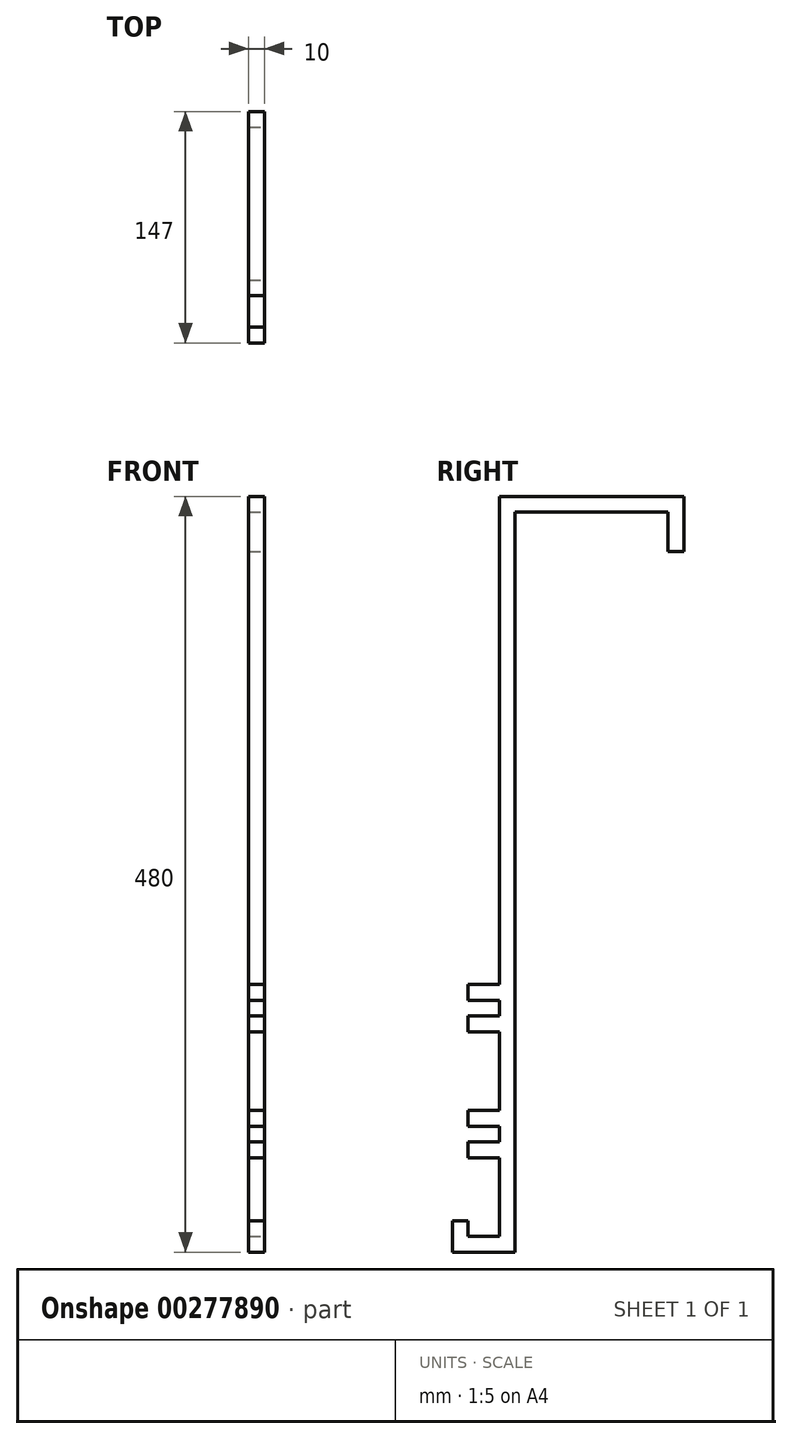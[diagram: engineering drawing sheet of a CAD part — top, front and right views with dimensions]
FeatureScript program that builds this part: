
annotation { "Feature Type Name" : "Feature", "Feature Type Description" : "" }
export const myFeature = defineFeature(function(context is Context, id is Id, definition is map)
    precondition{}
    {
        {
            var Q0;
            Q0=qCreatedBy(makeId("Right.planeOp"),FACE);
            var sketch = newSketch(context, id + "F0", { "sketchPlane" : qUnion([Q0])});
            skLineSegment(sketch, "E0", {"start": v(-6.6, 316.93) * mm, "end": v(-6.6, 6.93) * mm});
            skLineSegment(sketch, "E1", {"start": v(-6.6, 6.93) * mm, "end": v(-26.6, 6.93) * mm});
            skLineSegment(sketch, "E2", {"start": v(-26.6, 6.93) * mm, "end": v(-26.6, -3.07) * mm});
            skLineSegment(sketch, "E3", {"start": v(-26.6, -3.07) * mm, "end": v(-6.6, -3.07) * mm});
            skLineSegment(sketch, "E4", {"start": v(-6.6, -3.07) * mm, "end": v(-6.6, -13.07) * mm});
            skLineSegment(sketch, "E5", {"start": v(-6.6, -13.07) * mm, "end": v(-26.6, -13.07) * mm});
            skLineSegment(sketch, "E6", {"start": v(-26.6, -13.07) * mm, "end": v(-26.6, -23.07) * mm});
            skLineSegment(sketch, "E7", {"start": v(-26.6, -23.07) * mm, "end": v(-6.6, -23.07) * mm});
            skLineSegment(sketch, "E8", {"start": v(-6.6, -23.07) * mm, "end": v(-6.6, -73.07) * mm});
            skLineSegment(sketch, "E9", {"start": v(-6.6, -73.07) * mm, "end": v(-26.6, -73.07) * mm});
            skLineSegment(sketch, "E10", {"start": v(-26.6, -73.07) * mm, "end": v(-26.6, -83.07) * mm});
            skLineSegment(sketch, "E11", {"start": v(-26.6, -83.07) * mm, "end": v(-6.6, -83.07) * mm});
            skLineSegment(sketch, "E12", {"start": v(-6.6, -83.07) * mm, "end": v(-6.6, -93.07) * mm});
            skLineSegment(sketch, "E13", {"start": v(-6.6, -93.07) * mm, "end": v(-26.6, -93.07) * mm});
            skLineSegment(sketch, "E14", {"start": v(-26.6, -93.07) * mm, "end": v(-26.6, -103.07) * mm});
            skLineSegment(sketch, "E15", {"start": v(-26.6, -103.07) * mm, "end": v(-6.6, -103.07) * mm});
            skLineSegment(sketch, "E16", {"start": v(-6.6, -103.07) * mm, "end": v(-6.6, -153.07) * mm});
            skLineSegment(sketch, "E17", {"start": v(-6.6, -153.07) * mm, "end": v(-26.6, -153.07) * mm});
            skLineSegment(sketch, "E18", {"start": v(-26.6, -153.07) * mm, "end": v(-26.6, -143.07) * mm});
            skLineSegment(sketch, "E19", {"start": v(-26.6, -143.07) * mm, "end": v(-36.6, -143.07) * mm});
            skLineSegment(sketch, "E20", {"start": v(-36.6, -143.07) * mm, "end": v(-36.6, -163.07) * mm});
            skLineSegment(sketch, "E21", {"start": v(-6.6, 316.93) * mm, "end": v(110.4, 316.93) * mm});
            skLineSegment(sketch, "E22", {"start": v(110.4, 316.93) * mm, "end": v(110.4, 281.93) * mm});
            skLineSegment(sketch, "E23", {"start": v(110.4, 281.93) * mm, "end": v(100.4, 281.93) * mm});
            skLineSegment(sketch, "E24", {"start": v(100.4, 281.93) * mm, "end": v(100.4, 306.93) * mm});
            skLineSegment(sketch, "E25", {"start": v(100.4, 306.93) * mm, "end": v(3.4, 306.93) * mm});
            skLineSegment(sketch, "E26", {"start": v(-36.6, -163.07) * mm, "end": v(3.4, -163.07) * mm});
            skLineSegment(sketch, "E27", {"start": v(3.4, -163.07) * mm, "end": v(3.4, 306.93) * mm});
            skSolve(sketch);
        }
        {
            var Q0;
            Q0=qSketchRegion(id+"F0",true);
            extrude(context, id + "F1", {"entities" : qUnion([Q0]), "oppositeDirection" : true, "depth" : 10 * mm});
        }
    });
